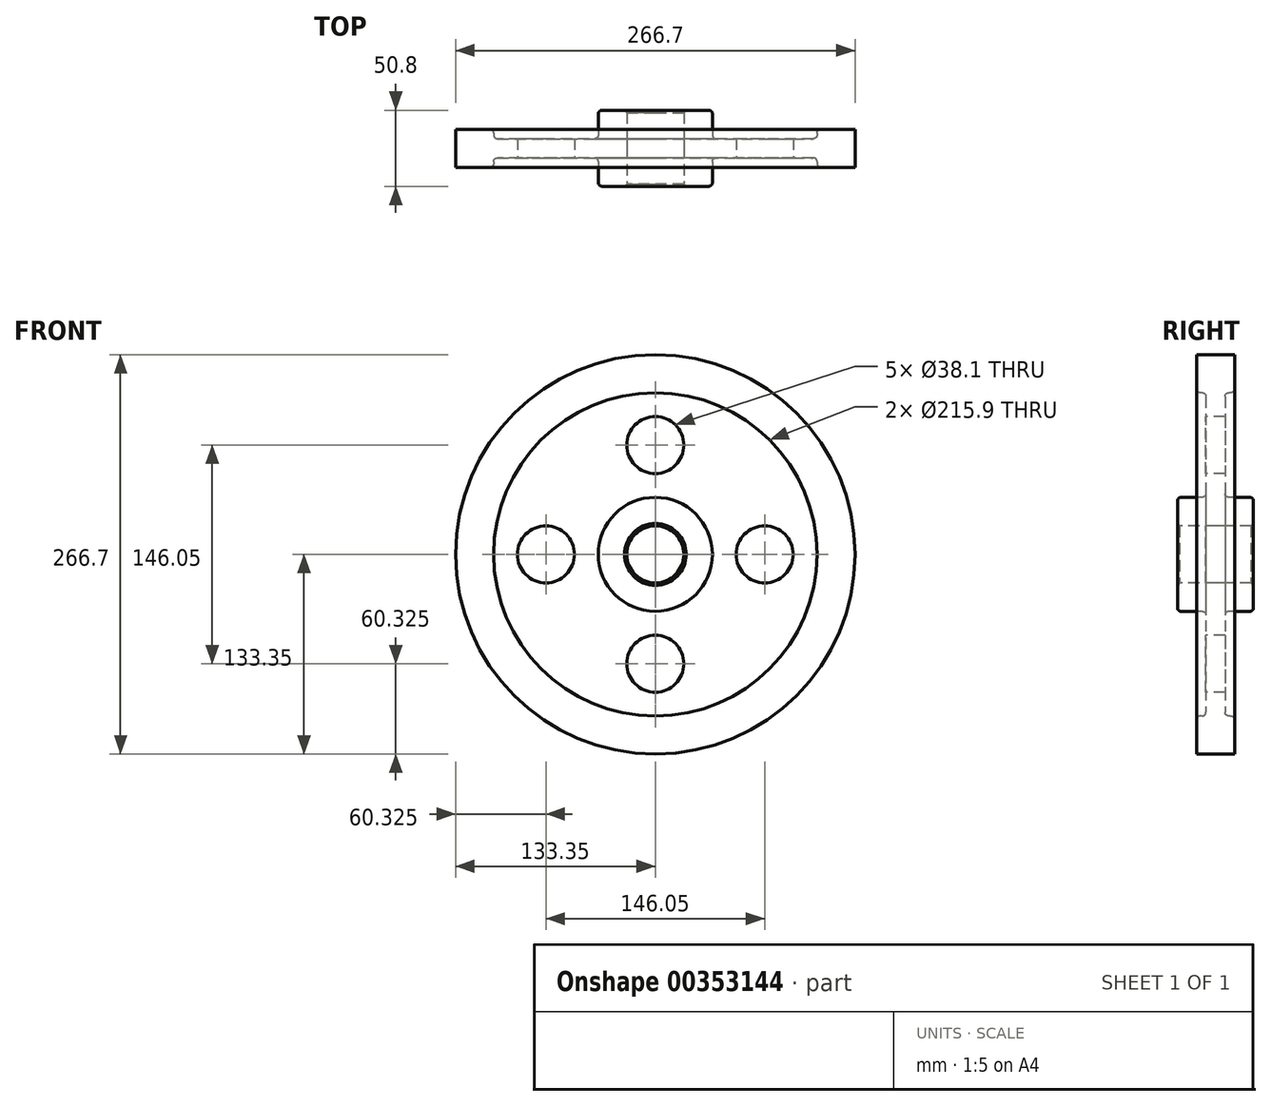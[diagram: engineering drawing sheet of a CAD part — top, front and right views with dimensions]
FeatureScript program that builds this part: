
annotation { "Feature Type Name" : "Feature", "Feature Type Description" : "" }
export const myFeature = defineFeature(function(context is Context, id is Id, definition is map)
    precondition{}
    {
        {
            var Q0;
            Q0=qCreatedBy(makeId("Right.planeOp"),FACE);
            var sketch = newSketch(context, id + "F0", { "sketchPlane" : qUnion([Q0])});
            skLineSegment(sketch, "E0", {"start": v(0, 0) * mm, "end": v(112.01, 0) * mm, "construction": true});
            skLineSegment(sketch, "E1.0", {"start": v(0, 19.05) * mm, "end": v(25.4, 19.05) * mm});
            skLineSegment(sketch, "E2.0", {"start": v(6.35, 38.1) * mm, "end": v(25.4, 38.1) * mm});
            skLineSegment(sketch, "E3.0", {"start": v(6.35, 107.95) * mm, "end": v(12.7, 107.95) * mm});
            skLineSegment(sketch, "E4.0", {"start": v(0, 133.35) * mm, "end": v(12.7, 133.35) * mm});
            skLineSegment(sketch, "E5", {"start": v(0, 133.35) * mm, "end": v(0, 0) * mm, "construction": true});
            skLineSegment(sketch, "E6.0", {"start": v(6.35, 107.95) * mm, "end": v(6.35, 38.1) * mm});
            skLineSegment(sketch, "E7.0", {"start": v(12.7, 133.35) * mm, "end": v(12.7, 107.95) * mm});
            skLineSegment(sketch, "E8.trimOffspring", {"start": v(25.4, 38.1) * mm, "end": v(25.4, 19.05) * mm});
            skLineSegment(sketch, "E9.MirrorCS", {"start": v(-12.7, 133.35) * mm, "end": v(-12.7, 107.95) * mm});
            skLineSegment(sketch, "E10.MirrorCS", {"start": v(-6.35, 107.95) * mm, "end": v(-6.35, 38.1) * mm});
            skLineSegment(sketch, "E11.MirrorCS", {"start": v(-6.35, 38.1) * mm, "end": v(-25.4, 38.1) * mm});
            skLineSegment(sketch, "E12.MirrorCS", {"start": v(-25.4, 38.1) * mm, "end": v(-25.4, 19.05) * mm});
            skLineSegment(sketch, "E13.MirrorCS", {"start": v(0, 19.05) * mm, "end": v(-25.4, 19.05) * mm});
            skLineSegment(sketch, "E14.MirrorCS", {"start": v(-6.35, 107.95) * mm, "end": v(-12.7, 107.95) * mm});
            skLineSegment(sketch, "E15.MirrorCS", {"start": v(0, 133.35) * mm, "end": v(-12.7, 133.35) * mm});
            skSolve(sketch);
        }
        {
            var Q0;
            Q0=makeQuery(id+"F0.imprint","IMPRINT",FACE,{"disambiguationData":[TD([[makeQuery(id+"F0.imprint","IMPRINT",EDGE,{"derivedFrom":sQuery(id+"F0.wireOp",EDGE,"E1.0")}),1.0]])]});
            var Q1;
            Q1=sQuery(id+"F0.wireOp",EDGE,"E0");
            revolve(context, id + "F1", {"entities" : qUnion([Q0]), "axis" : qUnion([Q1]), "revolveType" : RevolveType.FULL});
        }
        {
            var Q0;
            Q0=makeQuery(id+"F1.opRevolve","SWEPT_FACE",FACE,{"disambiguationData":[OSD([sQuery(id+"F0.wireOp",EDGE,"E10.MirrorCS")])]});
            var sketch = newSketch(context, id + "F2", { "sketchPlane" : qUnion([Q0])});
            skLineSegment(sketch, "E16", {"start": v(0, 0) * mm, "end": v(0, 73.03) * mm});
            skCircle(sketch, "E17", {"center": v(0, 73.03) * mm, "radius": 21.13 * mm});
            skCircle(sketch, "E18.1.0", {"center": v(-73.03, 0) * mm, "radius": 21.13 * mm});
            skCircle(sketch, "E18.2.0", {"center": v(0, -73.03) * mm, "radius": 21.13 * mm});
            skCircle(sketch, "E18.3.0", {"center": v(73.03, 0) * mm, "radius": 21.13 * mm});
            skPoint(sketch, "E18.center", {"position": v(0, 0) * mm});
            skSolve(sketch);
        }
        {
            var Q0;
            Q0=makeQuery(id+"F2.imprint","IMPRINT",FACE,{"disambiguationData":[TD([[makeQuery(id+"F2.imprint","IMPRINT",EDGE,{"derivedFrom":sQuery(id+"F2.wireOp",EDGE,"E18.1.0")}),1.0]])]});
            var Q1;
            Q1=makeQuery(id+"F2.imprint","IMPRINT",FACE,{"disambiguationData":[TD([[makeQuery(id+"F2.imprint","IMPRINT",EDGE,{"derivedFrom":sQuery(id+"F2.wireOp",EDGE,"E17")}),1.0]])]});
            var Q2;
            Q2=makeQuery(id+"F2.imprint","IMPRINT",FACE,{"disambiguationData":[TD([[makeQuery(id+"F2.imprint","IMPRINT",EDGE,{"derivedFrom":sQuery(id+"F2.wireOp",EDGE,"E18.3.0")}),1.0]])]});
            var Q3;
            Q3=makeQuery(id+"F2.imprint","IMPRINT",FACE,{"disambiguationData":[TD([[makeQuery(id+"F2.imprint","IMPRINT",EDGE,{"derivedFrom":sQuery(id+"F2.wireOp",EDGE,"E18.2.0")}),1.0]])]});
            extrude(context, id + "F3", {"entities" : qUnion([Q0, Q1, Q2, Q3]), "operationType" : NewBodyOperationType.REMOVE, "depth" : 25.4 * mm});
        }
        {
            var Q0;
            Q0=makeQuery(id+"F1.opRevolve","SWEPT_FACE",FACE,{"disambiguationData":[OSD([sQuery(id+"F0.wireOp",EDGE,"E10.MirrorCS")])]});
            var sketch = newSketch(context, id + "F4", { "sketchPlane" : qUnion([Q0])});
            skLineSegment(sketch, "E19", {"start": v(0, 0) * mm, "end": v(0, 73.03) * mm});
            skCircle(sketch, "E20", {"center": v(0, 73.03) * mm, "radius": 19.05 * mm});
            skCircle(sketch, "E21.1.0", {"center": v(-73.03, 0) * mm, "radius": 19.05 * mm});
            skCircle(sketch, "E21.2.0", {"center": v(0, -73.03) * mm, "radius": 19.05 * mm});
            skCircle(sketch, "E21.3.0", {"center": v(73.03, 0) * mm, "radius": 19.05 * mm});
            skPoint(sketch, "E21.center", {"position": v(0, 0) * mm});
            skSolve(sketch);
        }
        {
            var Q0;
            Q0=makeQuery(id+"F4.imprint","IMPRINT",FACE,{"disambiguationData":[TD([[makeQuery(id+"F4.imprint","IMPRINT",EDGE,{"derivedFrom":sQuery(id+"F4.wireOp",EDGE,"E21.2.0")}),1.0]])]});
            var Q1;
            Q1=makeQuery(id+"F4.imprint","IMPRINT",FACE,{"disambiguationData":[TD([[makeQuery(id+"F4.imprint","IMPRINT",EDGE,{"derivedFrom":sQuery(id+"F4.wireOp",EDGE,"E21.1.0")}),1.0]])]});
            var Q2;
            Q2=makeQuery(id+"F4.imprint","IMPRINT",FACE,{"disambiguationData":[TD([[makeQuery(id+"F4.imprint","IMPRINT",EDGE,{"derivedFrom":sQuery(id+"F4.wireOp",EDGE,"E21.3.0")}),1.0]])]});
            var Q3;
            Q3=makeQuery(id+"F4.imprint","IMPRINT",FACE,{"disambiguationData":[TD([[makeQuery(id+"F4.imprint","IMPRINT",EDGE,{"derivedFrom":sQuery(id+"F4.wireOp",EDGE,"E20")}),1.0]])]});
            extrude(context, id + "F5", {"entities" : qUnion([Q0, Q1, Q2, Q3]), "operationType" : NewBodyOperationType.REMOVE, "oppositeDirection" : true, "depth" : 25.4 * mm});
        }
        {
            var Q0;
            Q0=makeQuery(id+"F1.opRevolve","SWEPT_EDGE",EDGE,{"disambiguationData":[OSD([sQuery(id+"F0.wireOp",EDGE,"E9.MirrorCS"),sQuery(id+"F0.wireOp",EDGE,"E14.MirrorCS")])]});
            var Q1;
            Q1=makeQuery(id+"F1.opRevolve","SWEPT_EDGE",EDGE,{"disambiguationData":[OSD([sQuery(id+"F0.wireOp",EDGE,"E10.MirrorCS"),sQuery(id+"F0.wireOp",EDGE,"E14.MirrorCS")])]});
            var Q2;
            Q2=makeQuery(id+"F1.opRevolve","SWEPT_EDGE",EDGE,{"disambiguationData":[OSD([sQuery(id+"F0.wireOp",EDGE,"E11.MirrorCS"),sQuery(id+"F0.wireOp",EDGE,"E12.MirrorCS")])]});
            var Q3;
            Q3=makeQuery(id+"F1.opRevolve","SWEPT_EDGE",EDGE,{"disambiguationData":[OSD([sQuery(id+"F0.wireOp",EDGE,"E10.MirrorCS"),sQuery(id+"F0.wireOp",EDGE,"E11.MirrorCS")])]});
            fillet(context, id + "F6", {"entities" : qUnion([Q0, Q1, Q2, Q3]), "radius" : 2.54 * mm, "tangentPropagation" : true, "allowEdgeOverflow" : false});
        }
        {
            var Q0;
            Q0=makeQuery(id+"F1.opRevolve","SWEPT_EDGE",EDGE,{"disambiguationData":[OSD([sQuery(id+"F0.wireOp",EDGE,"E2.0"),sQuery(id+"F0.wireOp",EDGE,"E8.trimOffspring")])]});
            var Q1;
            Q1=makeQuery(id+"F1.opRevolve","SWEPT_EDGE",EDGE,{"disambiguationData":[OSD([sQuery(id+"F0.wireOp",EDGE,"E2.0"),sQuery(id+"F0.wireOp",EDGE,"E6.0")])]});
            var Q2;
            Q2=makeQuery(id+"F1.opRevolve","SWEPT_EDGE",EDGE,{"disambiguationData":[OSD([sQuery(id+"F0.wireOp",EDGE,"E3.0"),sQuery(id+"F0.wireOp",EDGE,"E6.0")])]});
            var Q3;
            Q3=makeQuery(id+"F1.opRevolve","SWEPT_EDGE",EDGE,{"disambiguationData":[OSD([sQuery(id+"F0.wireOp",EDGE,"E3.0"),sQuery(id+"F0.wireOp",EDGE,"E7.0")])]});
            fillet(context, id + "F7", {"entities" : qUnion([Q0, Q1, Q2, Q3]), "radius" : 2.54 * mm, "tangentPropagation" : true, "allowEdgeOverflow" : false});
        }
        {
            var Q0;
            Q0=makeQuery(id+"F1.opRevolve","SWEPT_EDGE",EDGE,{"disambiguationData":[OSD([sQuery(id+"F0.wireOp",EDGE,"E1.0"),sQuery(id+"F0.wireOp",EDGE,"E8.trimOffspring")])]});
            var Q1;
            Q1=makeQuery(id+"F1.opRevolve","SWEPT_EDGE",EDGE,{"disambiguationData":[OSD([sQuery(id+"F0.wireOp",EDGE,"E12.MirrorCS"),sQuery(id+"F0.wireOp",EDGE,"E13.MirrorCS")])]});
            chamfer(context, id + "F8", {"entities" : qUnion([Q0, Q1]), "width" : 1.59 * mm, "tangentPropagation" : true});
        }
    });
